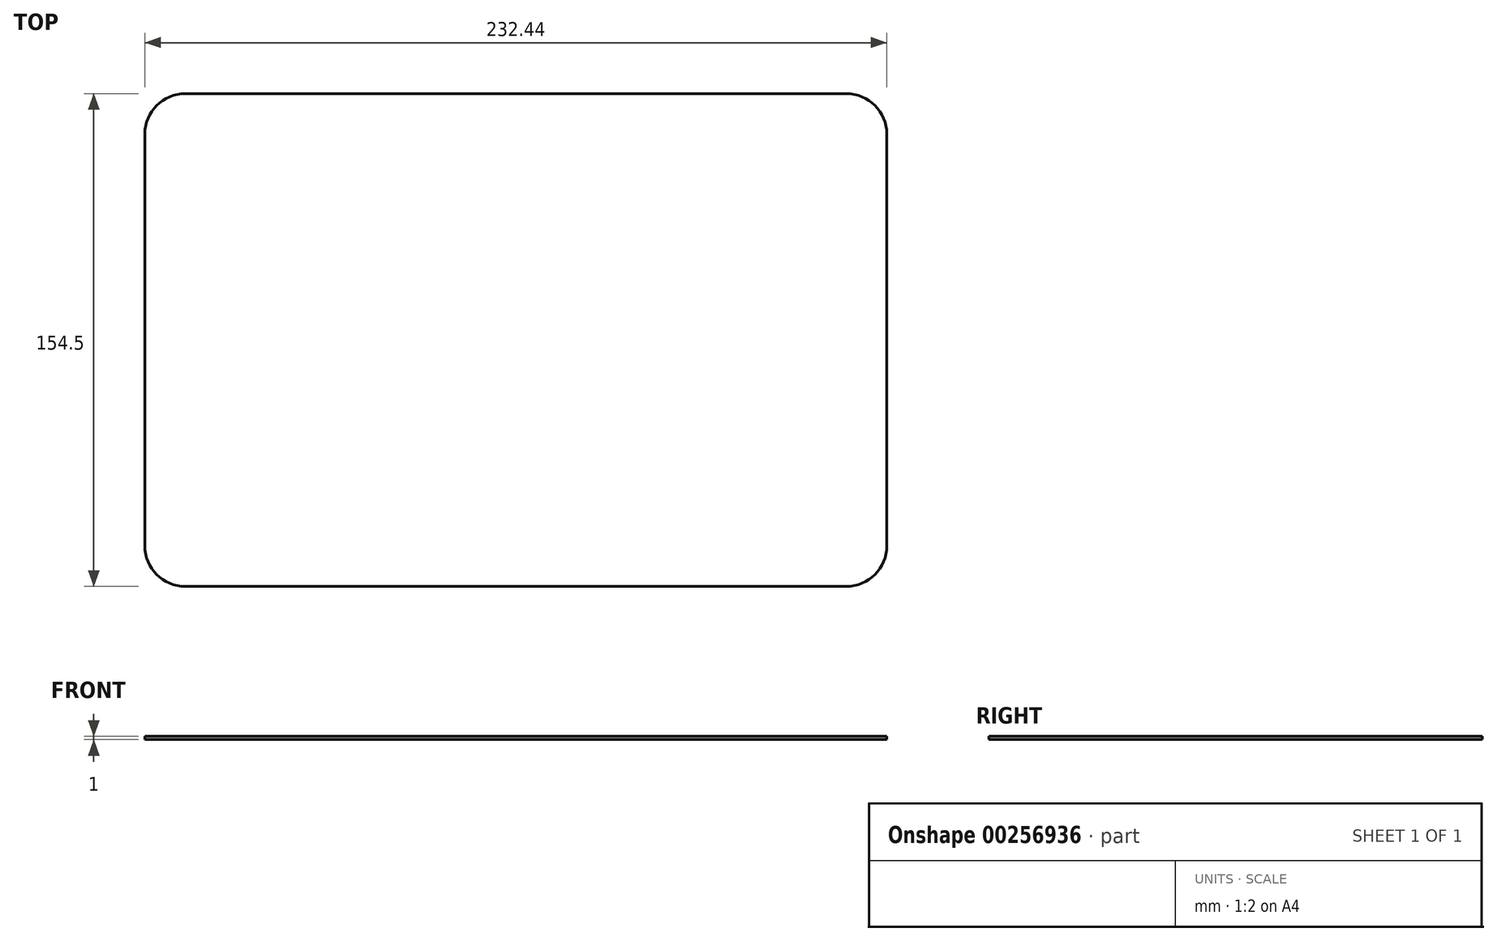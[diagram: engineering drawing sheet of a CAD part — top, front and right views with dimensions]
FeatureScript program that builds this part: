
annotation { "Feature Type Name" : "Feature", "Feature Type Description" : "" }
export const myFeature = defineFeature(function(context is Context, id is Id, definition is map)
    precondition{}
    {
        {
            var Q0;
            Q0=qCreatedBy(makeId("Top.planeOp"),FACE);
            var sketch = newSketch(context, id + "F0", { "sketchPlane" : qUnion([Q0])});
            skLineSegment(sketch, "E0.bottom", {"start": v(-103.52, 77.25) * mm, "end": v(103.52, 77.25) * mm});
            skLineSegment(sketch, "E0.top", {"start": v(-103.52, -77.25) * mm, "end": v(103.52, -77.25) * mm});
            skLineSegment(sketch, "E0.left", {"start": v(-116.22, 64.55) * mm, "end": v(-116.22, -64.55) * mm});
            skLineSegment(sketch, "E0.right", {"start": v(116.22, 64.55) * mm, "end": v(116.22, -64.55) * mm});
            skPoint(sketch, "E0.middle", {"position": v(0, 0) * mm});
            skPoint(sketch, "E1.visualSharp", {"position": v(-116.22, 77.25) * mm});
            skArc(sketch, "E1.filletArc", {"start": v(-103.52, 77.25) * mm, "mid": v(-112.5, 73.53) * mm, "end": v(-116.22, 64.55) * mm});
            skPoint(sketch, "E2.visualSharp", {"position": v(116.22, 77.25) * mm});
            skArc(sketch, "E2.filletArc", {"start": v(116.22, 64.55) * mm, "mid": v(112.5, 73.53) * mm, "end": v(103.52, 77.25) * mm});
            skPoint(sketch, "E3.visualSharp", {"position": v(116.22, -77.25) * mm});
            skArc(sketch, "E3.filletArc", {"start": v(103.52, -77.25) * mm, "mid": v(112.5, -73.53) * mm, "end": v(116.22, -64.55) * mm});
            skPoint(sketch, "E4.visualSharp", {"position": v(-116.22, -77.25) * mm});
            skArc(sketch, "E4.filletArc", {"start": v(-116.22, -64.55) * mm, "mid": v(-112.5, -73.53) * mm, "end": v(-103.52, -77.25) * mm});
            skSolve(sketch);
        }
        {
            var Q0;
            Q0 = qSketchRegion(id + "F0", true);
            extrude(context, id + "F1", {"entities" : qUnion([Q0]), "depth" : mm});
        }
    });
